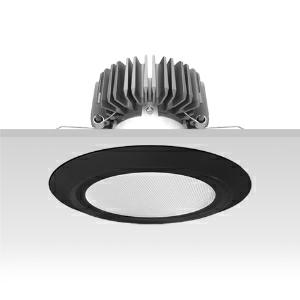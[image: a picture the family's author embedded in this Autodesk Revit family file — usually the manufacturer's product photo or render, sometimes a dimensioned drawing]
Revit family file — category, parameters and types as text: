
# Revit family: 3f_filippi_-_3f_reno_bianco_ampio_3f_filippi_-_30646_a01049_-_3f_reno_200_wh_2000-840_ep_wide___smp_bk_651f
name_source: partatom
category: Lighting Fixtures
units: mm (PartAtom-declared; Revit-internal decimal feet)

## family parameters
Cut with Voids When Loaded = No
Host = Face
Light Source = No
Part Type = Normal
Room Calculation Point = No
Round Connector Dimension = Use Diameter
Shared = No

## types (1)
- 3F Filippi - 3F Reno Bianco Ampio (1 x LED, 1723 lm, 21 W, 4000 K)
    Apparent Load = 21 VA
    Approval mark = ENEC
    CIE Flux Codes = 74 92 98 100 100
    Color Rendering = 80
    Color Temperature = 4000 K
    Control Gear = Electronic ballast
    Default Elevation = 1800 mm
    Description = ILLUMINOTECHNICAL
Luminous efficiency 100% (DLOR 100%, ULOR 0%).
Initial luminous flux of the luminaire 1723 lm.
Emergency luminaire luminous flux BLF 20%.
Direct symmetric wide distribution.
Installation Interdistance Transv.D = 1.06 x hu - Long.D = 1.04 x hu.
Average luminance <3000 cd/m² for radial angles >65°.
Tabular UGR (CIE 117 - 4H-8H; S=0.25H; 70/50/20): RUG 21.4 - 21.3.
Beam angle: 70° - 69°.
Luminous efficacy 82 lm/W.
Lifetime (L90/B10): 30000 h. (tq+25°C)
Lifetime (L85/B10): 50000 h. (tq+25°C)
Lifetime (L70/B10): 80000 h. (tq+25°C)
Sudden decreased luminous flux after 50000 hours: 0% (C0).
Photobiological safety in compliance with IEC/TR 62778: RG0 risk exempt, (IEC 62471).
In compliance with IEC/EN 62722-2-1 - IEC/EN 62717 standards.

SOURCE
Compact LED module 2000/840.
Energy efficiency class (UE 2019/2020 - UE 2019/2015): D.
CIE 13.3 Colour rendering index: CRI >80 (R9 <50%).
IES TM-30 Fidelity Index: Rf = 84 Rg = 95.
CCT nominal colour temperature 4000 K.
Colour initial tolerance (MacAdam): SDCM 3.
Zhaga Book 3 compliant.

MECHANICAL
Passive heat dissipator in die-casting aluminium, oversized, for optimum thermal management of the LED module.
Parabolic element with graduated/concentric rings in white polycarbonate.
Transparent external lens with glossy and satin differentiated surfaces, with a cooling and anti-insect system in methacrylate (PMMA).
Fastening spring clips in stainless steel.
Dimensions: diameter 226 mm, height 146 mm. Weight 1.475 kg.
IP44 protection degree for exposed part, IP20 for recessed part.
Mechanical strength to impacts IK05 (0.7 joule).
Glow-wire test resistance 650°C.

ELECTRICAL
Wiring on a separate unit.
Halogen Free electronic wiring 230V-50/60Hz, power factor 0.90, THD <25%, constant output current, SELV, class II, 1 driver.
Power of the luminaire 21 W.
CE - IEC 60598-1 - EN 60598-1.
EP maintained emergency wiring on board, 1h duration, 24h recharge; compliant with EN 60598-2-22, excluding high risk areas.
SAFE FLICKER: PstLM=<1 and SVM=<0.4 (IEC TR 61547-1 and IEC TR 63158), to ensure a more comfortable and safe light.
Ambient temperature from +5°C to +25°C.
Temperature class T6 max 85°C.
Relative humidity UR: <85%.

INSTALLATION
Pull-up recessed fitting.
False ceiling carving: 200 mm.
All accessories dedicated to this product are available on the Catalog and on our website www.3F-Filippi.com.

ACCESSORIES
A01049 - Anti-glare microprismatic SMP diffuser in methacrylate (PMMA), locked and in line with the trim, in black polycarbonate.

APPLICATIONS
Suitable product for food production plants (HACCP), IFS (Food Version 6), BRC (GSFS Food Version 7).
Environments: architectural, commercial, exhibition areas, transit areas, corridors, shops, display windows, service areas.
In false ceilings with narrow voids.

WARNING
Luminaire designed for disposal/recycling at end-of-life.
Replaceable (LED only) light source by a professional. Replaceable control gear by a professional.
    Height = 0 mm  [stored 0 ft]
    Lamp = 1 x LED
    Lamp Light Flux = 1723 lm
    Lamp Power = 21 W
    Lamp count = 1
    Length = 226 mm
    Lifetime = 50000 h
    Luminous efficacy = 82 lm/W
    Manufacturer = 3F Filippi
    ModVariant = No
    Model = 3F Filippi - 30646+A01049 - 3F Reno 200 WH 2000-840 EP WIDE + SMP BK
    Mounting Place = Ceiling
    Mounting Type = Recessed
    Number of Poles = 1
    OnlyDefault = Yes
    Power Factor = 1
    Product Name = 3F Filippi - 3F Reno Bianco Ampio
    Product group = recessed luminaire
    ProductGroupID = 4
    Protection Class = Protection class II
    Protection Degree = IP 20
    RLX_Detail_Level = 1
    RLX_Emergency_Light_Flux = 0 lm
    RLX_Emergency_Type = 0
    RLX_Emergency_Type_DB = No
    RlxData = <blob elided: 97889 chars, md5=72a60a18>
    Socket = socket
    Standby Power = 0 W
    System Light Flux = 1723 lm
    System Power = 21 W
    Type Comments = Product without accessories
    Type Image = 3ffilippi_3f_reno_200_bk_vs_smp.jpg
    URL = http://relux.com
    VarID = ---
    Voltage = 0 V
    Weight = 0.00 kg
    Width = 0 mm  [stored 0 ft]

note: [stored X ft] marks values corroborated as IEEE doubles in the binary element streams (Revit-internal decimal feet)

## geometry (parser evidence)
native form markers: Blend x4, Sweep x9
no freeform markers — native parametric forms only
